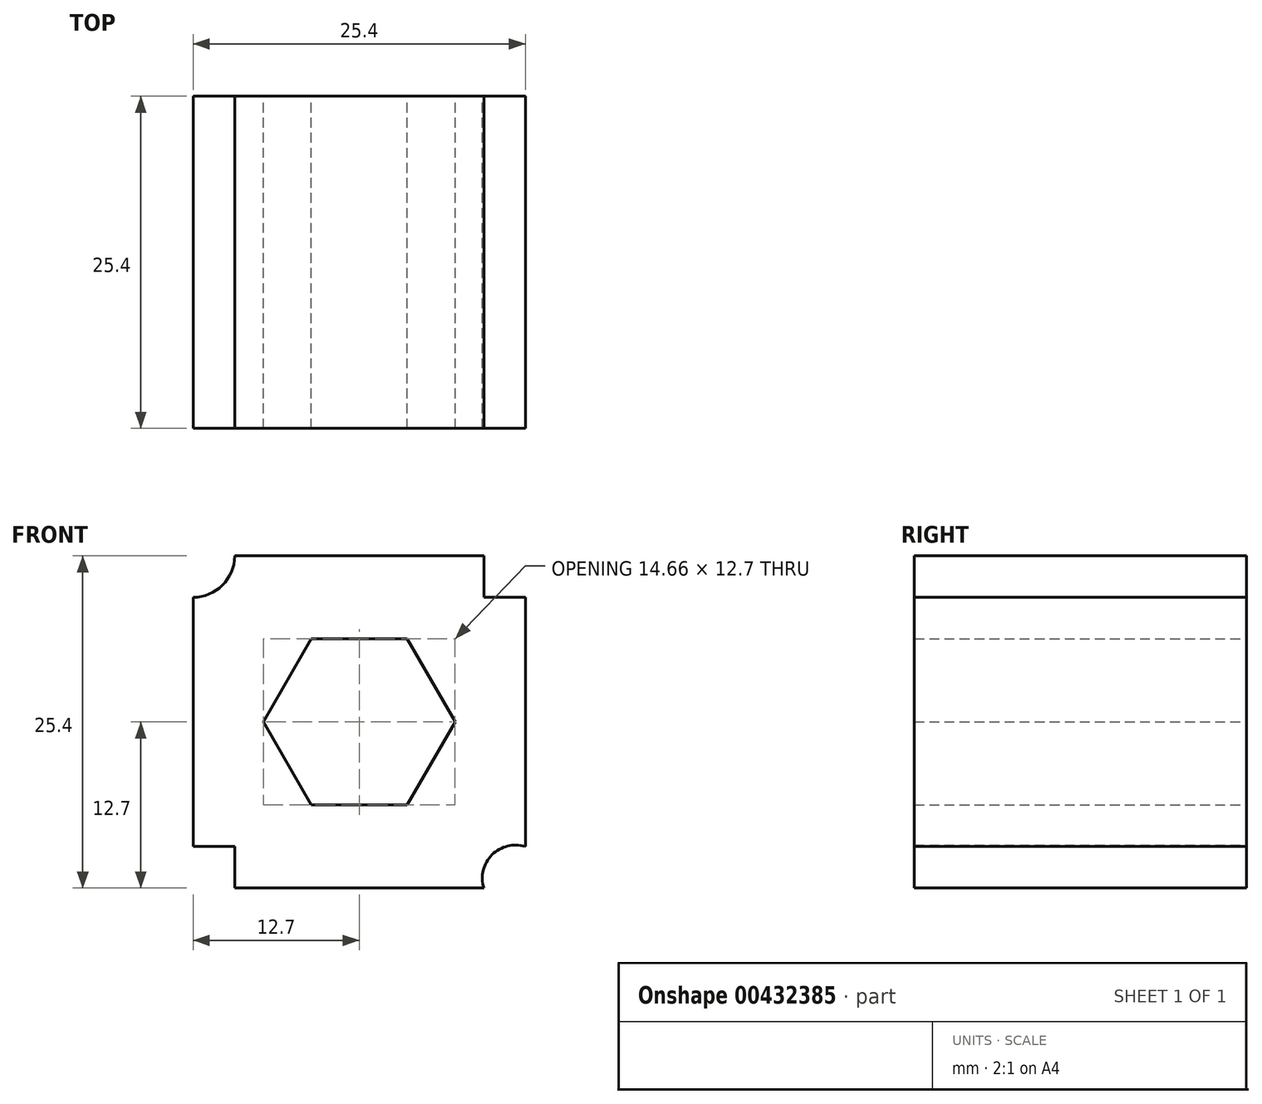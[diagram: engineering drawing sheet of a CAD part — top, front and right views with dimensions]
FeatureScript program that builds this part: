
annotation { "Feature Type Name" : "Feature", "Feature Type Description" : "" }
export const myFeature = defineFeature(function(context is Context, id is Id, definition is map)
    precondition{}
    {
        {
            var Q0;
            Q0=qCreatedBy(makeId("Front.planeOp"),FACE);
            var sketch = newSketch(context, id + "F0", { "sketchPlane" : qUnion([Q0])});
            skLineSegment(sketch, "E0.bottom", {"start": v(12.7, 12.7) * mm, "end": v(-12.7, 12.7) * mm});
            skLineSegment(sketch, "E0.top", {"start": v(12.7, -12.7) * mm, "end": v(-12.7, -12.7) * mm});
            skLineSegment(sketch, "E0.left", {"start": v(12.7, 12.7) * mm, "end": v(12.7, -12.7) * mm});
            skLineSegment(sketch, "E0.right", {"start": v(-12.7, 12.7) * mm, "end": v(-12.7, -12.7) * mm});
            skPoint(sketch, "E0.middle", {"position": v(0, 0) * mm});
            skLineSegment(sketch, "E1.bottom", {"start": v(9.53, 9.53) * mm, "end": v(12.7, 9.53) * mm});
            skLineSegment(sketch, "E1.left", {"start": v(9.53, 9.53) * mm, "end": v(9.53, 12.7) * mm});
            skPoint(sketch, "E1.middle", {"position": v(12.7, 12.7) * mm});
            skLineSegment(sketch, "E2.top", {"start": v(-12.7, -9.52) * mm, "end": v(-9.52, -9.52) * mm});
            skLineSegment(sketch, "E2.right", {"start": v(-9.52, -12.7) * mm, "end": v(-9.52, -9.52) * mm});
            skPoint(sketch, "E2.middle", {"position": v(-12.7, -12.7) * mm});
            skPoint(sketch, "E1.right.end.orphan", {"position": v(15.88, 15.88) * mm});
            skPoint(sketch, "E3.orphan", {"position": v(9.53, 15.88) * mm});
            skPoint(sketch, "E4.orphan", {"position": v(15.88, 9.53) * mm});
            skPoint(sketch, "E2.bottom.end.orphan", {"position": v(-9.52, -15.88) * mm});
            skPoint(sketch, "E2.left.end.orphan", {"position": v(-15.88, -9.52) * mm});
            skPoint(sketch, "E2.left.start.orphan", {"position": v(-15.88, -15.88) * mm});
            skPoint(sketch, "E5", {"position": v(-9.52, 12.7) * mm});
            skPoint(sketch, "E6", {"position": v(9.52, -12.7) * mm});
            skPoint(sketch, "E7", {"position": v(-12.7, 9.52) * mm});
            skPoint(sketch, "E8", {"position": v(12.7, -9.52) * mm});
            skArc(sketch, "E9", {"start": v(-12.7, 9.52) * mm, "mid": v(-10.45, 10.45) * mm, "end": v(-9.52, 12.7) * mm});
            skArc(sketch, "E10", {"start": v(12.7, -9.52) * mm, "mid": v(10.16, -10.16) * mm, "end": v(9.52, -12.7) * mm});
            skCircle(sketch, "E11.cCircle", {"center": v(0, 0) * mm, "radius": 6.35 * mm, "construction": true});
            skLineSegment(sketch, "E11.0", {"start": v(3.67, 6.35) * mm, "end": v(7.33, 0) * mm});
            skLineSegment(sketch, "E11.1", {"start": v(7.33, 0) * mm, "end": v(3.67, -6.35) * mm});
            skLineSegment(sketch, "E11.2", {"start": v(3.67, -6.35) * mm, "end": v(-3.67, -6.35) * mm});
            skLineSegment(sketch, "E11.3", {"start": v(-3.67, -6.35) * mm, "end": v(-7.33, 0) * mm});
            skLineSegment(sketch, "E11.4", {"start": v(-7.33, 0) * mm, "end": v(-3.67, 6.35) * mm});
            skLineSegment(sketch, "E11.5", {"start": v(-3.67, 6.35) * mm, "end": v(3.67, 6.35) * mm});
            skPoint(sketch, "E11.0.midPoint", {"position": v(5.5, 3.18) * mm});
            skSolve(sketch);
        }
        {
            var Q0;
            {var subQ4=sQuery(id+"F0.wireOp",EDGE,"E1.bottom");Q0=makeQuery(id+"F0.imprint","IMPRINT",FACE,{"disambiguationData":[TD([[makeQuery(id+"F0.imprint","IMPRINT",EDGE,{"derivedFrom":subQ4}),-1.0]])]});}
            extrude(context, id + "F1", {"entities" : qUnion([Q0]), "depth" : 25.4 * mm});
        }
    });
